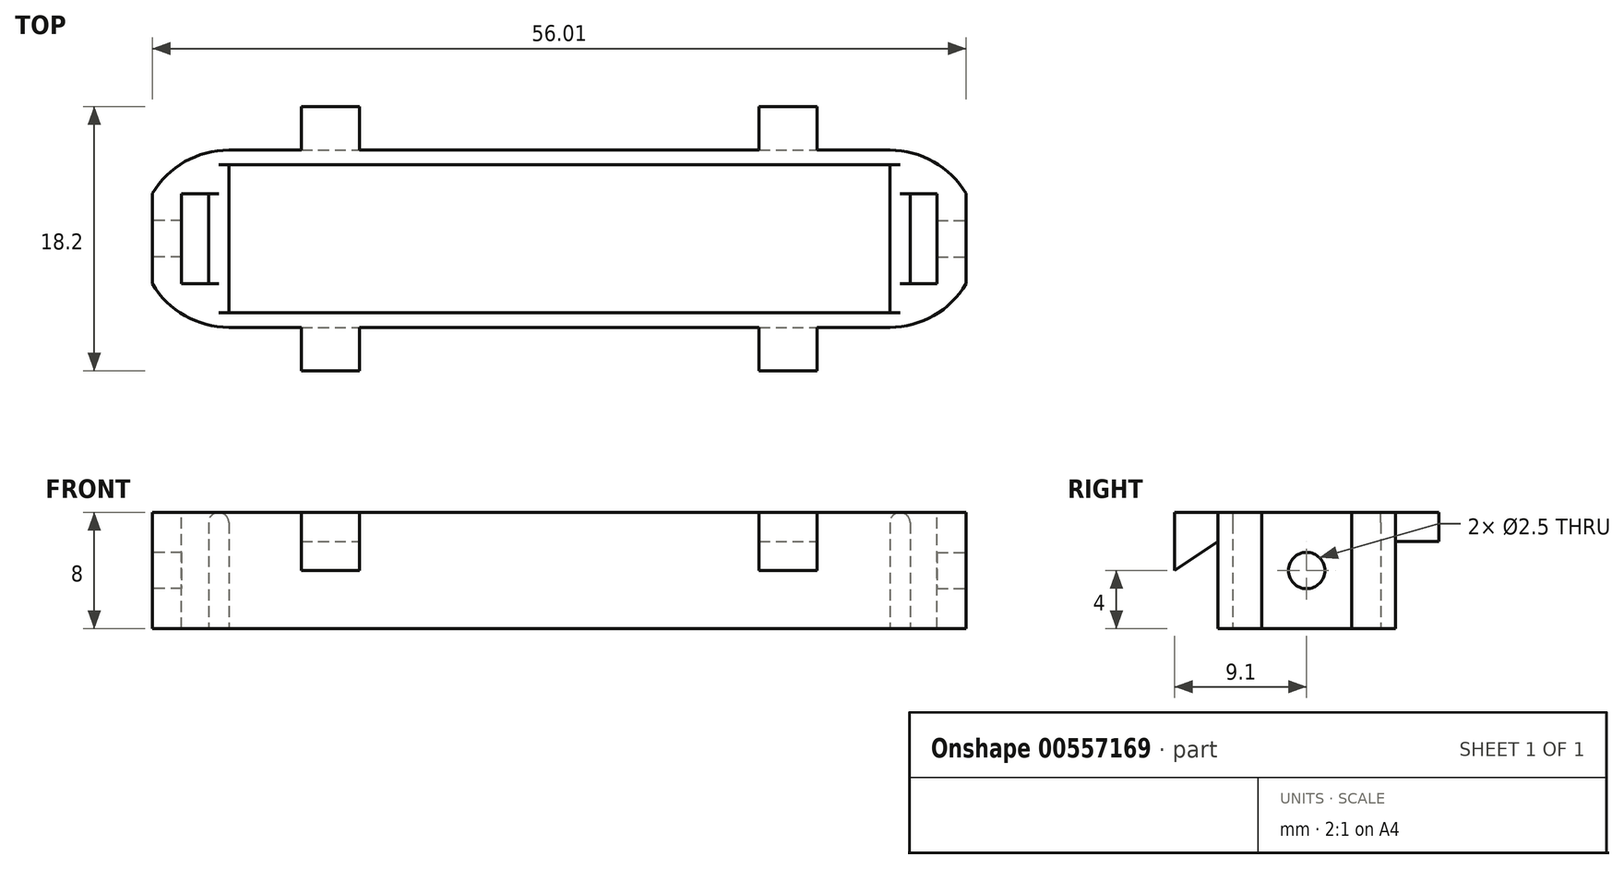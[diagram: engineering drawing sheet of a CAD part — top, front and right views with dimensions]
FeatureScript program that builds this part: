
annotation { "Feature Type Name" : "Feature", "Feature Type Description" : "" }
export const myFeature = defineFeature(function(context is Context, id is Id, definition is map)
    precondition{}
    {
        {
            var Q0;
            Q0=qCreatedBy(makeId("Top.planeOp"),FACE);
            var sketch = newSketch(context, id + "F0", { "sketchPlane" : qUnion([Q0])});
            skLineSegment(sketch, "E0", {"start": v(-58.41, 47.87) * mm, "end": v(-56.91, 47.87) * mm});
            skLineSegment(sketch, "E1", {"start": v(-58.41, 41.67) * mm, "end": v(-56.91, 41.67) * mm});
            skLineSegment(sketch, "E2.trimOffspring", {"start": v(-58.41, 41.67) * mm, "end": v(-58.41, 47.87) * mm});
            skLineSegment(sketch, "E3.trimOffspring", {"start": v(-56.91, 41.67) * mm, "end": v(-56.91, 47.87) * mm});
            skPoint(sketch, "E4", {"position": v(-55.91, 39.67) * mm});
            skPoint(sketch, "E5", {"position": v(-58.41, 44.77) * mm});
            skPoint(sketch, "E6", {"position": v(-55.91, 50.87) * mm});
            skLineSegment(sketch, "E7.MirrorCS", {"start": v(-7.91, 41.67) * mm, "end": v(-9.41, 41.67) * mm});
            skLineSegment(sketch, "E8.MirrorCS", {"start": v(-7.91, 47.87) * mm, "end": v(-9.41, 47.87) * mm});
            skLineSegment(sketch, "E9.MirrorCS", {"start": v(-9.41, 41.67) * mm, "end": v(-9.41, 47.87) * mm});
            skLineSegment(sketch, "E10.MirrorCS", {"start": v(-7.91, 41.67) * mm, "end": v(-7.91, 47.87) * mm});
            skPoint(sketch, "E11.MirrorP", {"position": v(-10.41, 39.67) * mm});
            skPoint(sketch, "E12.MirrorP", {"position": v(-10.41, 50.87) * mm});
            skLineSegment(sketch, "E13", {"start": v(-55.91, 49.87) * mm, "end": v(-10.41, 49.87) * mm});
            skLineSegment(sketch, "E14", {"start": v(-55.91, 50.87) * mm, "end": v(-10.41, 50.87) * mm});
            skLineSegment(sketch, "E15", {"start": v(-55.91, 49.87) * mm, "end": v(-55.91, 39.67) * mm});
            skLineSegment(sketch, "E16", {"start": v(-10.41, 49.87) * mm, "end": v(-10.41, 39.67) * mm});
            skPoint(sketch, "E17", {"position": v(-56.91, 44.77) * mm});
            skPoint(sketch, "E18", {"position": v(-55.91, 44.77) * mm});
            skPoint(sketch, "E19", {"position": v(-9.41, 44.77) * mm});
            skPoint(sketch, "E20", {"position": v(-10.41, 44.77) * mm});
            skLineSegment(sketch, "E21", {"start": v(-55.91, 39.67) * mm, "end": v(-10.41, 39.67) * mm});
            skLineSegment(sketch, "E22", {"start": v(-55.91, 38.67) * mm, "end": v(-10.41, 38.67) * mm});
            skPoint(sketch, "E23", {"position": v(-7.91, 44.77) * mm});
            skPoint(sketch, "E24", {"position": v(-55.91, 38.67) * mm});
            skPoint(sketch, "E25", {"position": v(-10.41, 38.67) * mm});
            skPoint(sketch, "E26", {"position": v(-10.41, 49.87) * mm});
            skPoint(sketch, "E27", {"position": v(-55.91, 49.87) * mm});
            skArc(sketch, "E28", {"start": v(-55.91, 50.87) * mm, "mid": v(-58.94, 50.07) * mm, "end": v(-61.17, 47.88) * mm});
            skArc(sketch, "E29", {"start": v(-10.41, 38.67) * mm, "mid": v(-7.4, 39.47) * mm, "end": v(-5.16, 41.67) * mm});
            skLineSegment(sketch, "E30", {"start": v(-61.17, 47.88) * mm, "end": v(-61.17, 41.67) * mm});
            skPoint(sketch, "E31", {"position": v(-33.16, 50.87) * mm});
            skPoint(sketch, "E32", {"position": v(-33.16, 38.67) * mm});
            skLineSegment(sketch, "E33", {"start": v(-33.16, 50.87) * mm, "end": v(-33.16, 38.67) * mm, "construction": true});
            skLineSegment(sketch, "E34.MirrorCS", {"start": v(-5.16, 47.88) * mm, "end": v(-5.16, 41.67) * mm});
            skArc(sketch, "E35.trimOffspring", {"start": v(-61.17, 41.67) * mm, "mid": v(-58.94, 39.47) * mm, "end": v(-55.91, 38.67) * mm});
            skArc(sketch, "E36.trimOffspring", {"start": v(-5.16, 47.88) * mm, "mid": v(-7.4, 50.07) * mm, "end": v(-10.41, 50.87) * mm});
            skLineSegment(sketch, "E37", {"start": v(-55.91, 44.77) * mm, "end": v(-10.41, 44.77) * mm, "construction": true});
            skSolve(sketch);
        }
        {
            var Q0;
            Q0=makeQuery(id+"F0.imprint","IMPRINT",FACE,{"disambiguationData":[TD([[makeQuery(id+"F0.imprint","IMPRINT",EDGE,{"derivedFrom":sQuery(id+"F0.wireOp",EDGE,"E0")}),1.0]])]});
            extrude(context, id + "F1", {"entities" : qUnion([Q0]), "depth" : 8 * mm, "offsetDistance" : 25 * mm});
        }
        {
            var Q0;
            Q0=makeQuery(id+"F1.opExtrude","SWEPT_FACE",FACE,{"disambiguationData":[OSD([sQuery(id+"F0.wireOp",EDGE,"E34.MirrorCS")])]});
            var sketch = newSketch(context, id + "F2", { "sketchPlane" : qUnion([Q0])});
            skPoint(sketch, "E38.0", {"position": v(44.77, 0) * mm});
            skPoint(sketch, "E38.2", {"position": v(44.77, 0) * mm});
            skCircle(sketch, "E39", {"center": v(44.77, 4) * mm, "radius": 1.25 * mm});
            skPoint(sketch, "E39.centerSnap0", {"position": v(45.62, 4) * mm});
            skSolve(sketch);
        }
        {
            var Q0;
            Q0=makeQuery(id+"F1.opExtrude","SWEPT_FACE",FACE,{"disambiguationData":[OSD([sQuery(id+"F0.wireOp",EDGE,"E30")])]});
            var sketch = newSketch(context, id + "F3", { "sketchPlane" : qUnion([Q0])});
            skPoint(sketch, "E40.0", {"position": v(-44.77, 0) * mm});
            skPoint(sketch, "E41.0", {"position": v(-45.62, 4) * mm});
            skCircle(sketch, "E42", {"center": v(-44.77, 4) * mm, "radius": 1.25 * mm});
            skSolve(sketch);
        }
        {
            var Q0;
            Q0=makeQuery(id+"F3.imprint","IMPRINT",FACE,{"disambiguationData":[TD([[makeQuery(id+"F3.imprint","IMPRINT",EDGE,{"derivedFrom":sQuery(id+"F3.wireOp",EDGE,"E42")}),1.0]])]});
            extrude(context, id + "F4", {"entities" : qUnion([Q0]), "operationType" : NewBodyOperationType.REMOVE, "oppositeDirection" : true, "depth" : 3 * mm, "offsetDistance" : 25 * mm});
        }
        {
            var Q0;
            Q0=makeQuery(id+"F2.imprint","IMPRINT",FACE,{"disambiguationData":[TD([[makeQuery(id+"F2.imprint","IMPRINT",EDGE,{"derivedFrom":sQuery(id+"F2.wireOp",EDGE,"E39")}),1.0]])]});
            extrude(context, id + "F5", {"entities" : qUnion([Q0]), "operationType" : NewBodyOperationType.REMOVE, "oppositeDirection" : true, "depth" : 3 * mm, "offsetDistance" : 25 * mm});
        }
        {
            var Q0;
            Q0=makeQuery(id+"F1.opExtrude","CAP_FACE",FACE,{"disambiguationData":[OSD([sQuery(id+"F0.wireOp",EDGE,"5c85485d-57c3-49a4-9234-01fc0bf89ff7.left"),sQuery(id+"F0.wireOp",EDGE,"5c85485d-57c3-49a4-9234-01fc0bf89ff7.right"),sQuery(id+"F0.wireOp",EDGE,"E0"),sQuery(id+"F0.wireOp",EDGE,"E1"),sQuery(id+"F0.wireOp",EDGE,"f26dac97-f157-4d3b-b19c-ac2ae7369aeb.MirrorCS"),sQuery(id+"F0.wireOp",EDGE,"fdaca539-c827-4bf9-9b72-cb5319b9078c.MirrorCS"),sQuery(id+"F0.wireOp",EDGE,"E2.trimOffspring"),sQuery(id+"F0.wireOp",EDGE,"E3.trimOffspring"),sQuery(id+"F0.wireOp",EDGE,"773fe0d1-a9d3-4c5f-a97c-df7c8a0fcf99"),sQuery(id+"F0.wireOp",EDGE,"c1d238ae-af6c-4615-ba33-6711a1cbf2eb.MirrorCS"),sQuery(id+"F0.wireOp",EDGE,"24cf176b-f46d-4737-b83f-17166a3a977d"),sQuery(id+"F0.wireOp",EDGE,"930f735f-535e-48a8-9612-ca19f04ff2fe.MirrorCS"),sQuery(id+"F0.wireOp",EDGE,"54351eae-afcf-4464-b00b-301f5b7c95d1.MirrorCS"),sQuery(id+"F0.wireOp",EDGE,"E7.MirrorCS"),sQuery(id+"F0.wireOp",EDGE,"E8.MirrorCS"),sQuery(id+"F0.wireOp",EDGE,"E10.MirrorCS"),sQuery(id+"F0.wireOp",EDGE,"2c25c5c6-e33a-4382-b5a6-a77b0c508d72.MirrorCS"),sQuery(id+"F0.wireOp",EDGE,"f8cf7686-dc48-4d1f-ad7e-551f82504d00.MirrorCS"),sQuery(id+"F0.wireOp",EDGE,"E9.MirrorCS"),sQuery(id+"F0.wireOp",EDGE,"bb7f4395-c74a-4e4d-ba5c-67a6b84b5c23.MirrorCS"),sQuery(id+"F0.wireOp",EDGE,"2b76229e-1219-44ec-801c-a60a5f2764bf.MirrorCS"),sQuery(id+"F0.wireOp",EDGE,"5ebec35d-3fc7-4fed-b7fb-ec59319a5e31.MirrorCS"),sQuery(id+"F0.wireOp",EDGE,"E13"),sQuery(id+"F0.wireOp",EDGE,"E14"),sQuery(id+"F0.wireOp",EDGE,"nzgn4MnC-cCwg-rH8m-cCMt-Htn1G1sgsl9W"),sQuery(id+"F0.wireOp",EDGE,"OD229cqR-pfQO-gkFn-DRH1-wKdn3JZuODgv"),sQuery(id+"F0.wireOp",EDGE,"E15"),sQuery(id+"F0.wireOp",EDGE,"E16")])],"isStart":false});
            var sketch = newSketch(context, id + "F6", { "sketchPlane" : qUnion([Q0])});
            skPoint(sketch, "E43", {"position": v(-33.16, 50.87) * mm});
            skLineSegment(sketch, "E44", {"start": v(-55.91, 44.77) * mm, "end": v(-10.41, 44.77) * mm, "construction": true});
            skPoint(sketch, "E45.0", {"position": v(-55.91, 50.87) * mm});
            skPoint(sketch, "E45.1", {"position": v(-10.41, 50.87) * mm});
            skPoint(sketch, "E46", {"position": v(-17.41, 50.87) * mm});
            skPoint(sketch, "E47", {"position": v(-48.91, 50.87) * mm});
            skLineSegment(sketch, "E48", {"start": v(-19.41, 53.87) * mm, "end": v(-19.41, 50.87) * mm});
            skLineSegment(sketch, "E49", {"start": v(-15.41, 53.87) * mm, "end": v(-15.41, 50.87) * mm});
            skLineSegment(sketch, "E50", {"start": v(-19.41, 53.87) * mm, "end": v(-15.41, 53.87) * mm});
            skLineSegment(sketch, "E51.MirrorCS", {"start": v(-15.41, 35.67) * mm, "end": v(-15.41, 38.67) * mm});
            skLineSegment(sketch, "E52.MirrorCS", {"start": v(-19.41, 35.67) * mm, "end": v(-19.41, 38.67) * mm});
            skLineSegment(sketch, "E53.MirrorCS", {"start": v(-19.41, 35.67) * mm, "end": v(-15.41, 35.67) * mm});
            skLineSegment(sketch, "E54.MirrorCS", {"start": v(-46.91, 53.87) * mm, "end": v(-46.91, 50.87) * mm});
            skLineSegment(sketch, "E55.MirrorCS", {"start": v(-46.91, 53.87) * mm, "end": v(-50.91, 53.87) * mm});
            skLineSegment(sketch, "E56.MirrorCS", {"start": v(-50.91, 53.87) * mm, "end": v(-50.91, 50.87) * mm});
            skLineSegment(sketch, "E57.MirrorCS", {"start": v(-50.91, 35.67) * mm, "end": v(-50.91, 38.67) * mm});
            skLineSegment(sketch, "E58.MirrorCS", {"start": v(-46.91, 35.67) * mm, "end": v(-50.91, 35.67) * mm});
            skLineSegment(sketch, "E59.MirrorCS", {"start": v(-46.91, 35.67) * mm, "end": v(-46.91, 38.67) * mm});
            skSolve(sketch);
        }
        {
            var Q0;
            {var subQ0=sQuery(id+"F6.wireOp",EDGE,"E48");Q0=makeQuery(id+"F6.imprint","IMPRINT",FACE,{"disambiguationData":[TD([[makeQuery(id+"F6.imprint","IMPRINT",EDGE,{"derivedFrom":subQ0}),1.0]])]});}
            var Q1;
            {var subQ0=sQuery(id+"F6.wireOp",EDGE,"E54.MirrorCS");Q1=makeQuery(id+"F6.imprint","IMPRINT",FACE,{"disambiguationData":[TD([[makeQuery(id+"F6.imprint","IMPRINT",EDGE,{"derivedFrom":subQ0}),-1.0]])]});}
            var Q2;
            {var subQ0=sQuery(id+"F6.wireOp",EDGE,"E57.MirrorCS");Q2=makeQuery(id+"F6.imprint","IMPRINT",FACE,{"disambiguationData":[TD([[makeQuery(id+"F6.imprint","IMPRINT",EDGE,{"derivedFrom":subQ0}),-1.0]])]});}
            var Q3;
            {var subQ0=sQuery(id+"F6.wireOp",EDGE,"E51.MirrorCS");Q3=makeQuery(id+"F6.imprint","IMPRINT",FACE,{"disambiguationData":[TD([[makeQuery(id+"F6.imprint","IMPRINT",EDGE,{"derivedFrom":subQ0}),1.0]])]});}
            extrude(context, id + "F7", {"entities" : qUnion([Q0, Q1, Q2, Q3]), "operationType" : NewBodyOperationType.ADD, "oppositeDirection" : true, "depth" : 2 * mm, "offsetDistance" : 25 * mm});
        }
        {
            var Q0;
            Q0=makeQuery(id+"F7.opExtrude","SWEPT_FACE",FACE,{"disambiguationData":[OSD([sQuery(id+"F6.wireOp",EDGE,"E51.MirrorCS")])]});
            var sketch = newSketch(context, id + "F8", { "sketchPlane" : qUnion([Q0])});
            skPoint(sketch, "E60", {"position": v(35.67, 4) * mm});
            skLineSegment(sketch, "E61", {"start": v(35.67, 6) * mm, "end": v(35.67, 4) * mm});
            skLineSegment(sketch, "E62", {"start": v(35.67, 4) * mm, "end": v(38.67, 6) * mm});
            skSolve(sketch);
        }
        {
            var Q0;
            Q0=makeQuery(id+"F8.imprint","IMPRINT",FACE,{"disambiguationData":[TD([[makeQuery(id+"F8.imprint","IMPRINT",EDGE,{"derivedFrom":sQuery(id+"F8.wireOp",EDGE,"E61")}),1.0]])]});
            extrude(context, id + "F9", {"entities" : qUnion([Q0]), "operationType" : NewBodyOperationType.ADD, "oppositeDirection" : true, "depth" : 4 * mm, "offsetDistance" : 25 * mm});
        }
        {
            var Q0;
            Q0=sQuery(id+"F6.wireOp",EDGE,"E44");
            cPlane(context, id + "F10", {"entities" : qUnion([Q0]), "cplaneType" : CPlaneType.LINE_ANGLE, "offset" : 25 * mm, "angle" : 0 * degree, "width" : 150 * mm, "height" : 150 * mm});
        }
        {
            var Q0;
            Q0=makeQuery(id+"F7.opExtrude","SWEPT_FACE",FACE,{"disambiguationData":[OSD([sQuery(id+"F6.wireOp",EDGE,"E57.MirrorCS")])]});
            var sketch = newSketch(context, id + "F11", { "sketchPlane" : qUnion([Q0])});
            skPoint(sketch, "E63", {"position": v(-35.67, 4) * mm});
            skLineSegment(sketch, "E64", {"start": v(-35.67, 4) * mm, "end": v(-35.67, 6) * mm});
            skLineSegment(sketch, "E65", {"start": v(-35.67, 4) * mm, "end": v(-38.67, 6) * mm});
            skSolve(sketch);
        }
        {
            var Q0;
            Q0=makeQuery(id+"F11.imprint","IMPRINT",FACE,{"disambiguationData":[TD([[makeQuery(id+"F11.imprint","IMPRINT",EDGE,{"derivedFrom":sQuery(id+"F11.wireOp",EDGE,"E64")}),1.0]])]});
            extrude(context, id + "F12", {"entities" : qUnion([Q0]), "operationType" : NewBodyOperationType.ADD, "oppositeDirection" : true, "depth" : 4 * mm, "offsetDistance" : 25 * mm});
        }
        {
            var Q0;
            {var subQ0=sQuery(id+"F0.wireOp",EDGE,"E22");var subQ1=sQuery(id+"F0.wireOp",EDGE,"E14");Q0=makeQuery(id+"F7.boolean.opBoolean","MERGE",FACE,{"derivedFrom":[makeQuery(id+"F1.opExtrude","CAP_FACE",FACE,{"disambiguationData":[OSD([sQuery(id+"F0.wireOp",EDGE,"E0"),sQuery(id+"F0.wireOp",EDGE,"E1"),sQuery(id+"F0.wireOp",EDGE,"E2.trimOffspring"),sQuery(id+"F0.wireOp",EDGE,"E3.trimOffspring"),sQuery(id+"F0.wireOp",EDGE,"E7.MirrorCS"),sQuery(id+"F0.wireOp",EDGE,"E8.MirrorCS"),sQuery(id+"F0.wireOp",EDGE,"E10.MirrorCS"),sQuery(id+"F0.wireOp",EDGE,"E9.MirrorCS"),sQuery(id+"F0.wireOp",EDGE,"E13"),subQ1,sQuery(id+"F0.wireOp",EDGE,"E15"),sQuery(id+"F0.wireOp",EDGE,"E16"),sQuery(id+"F0.wireOp",EDGE,"E21"),subQ0,sQuery(id+"F0.wireOp",EDGE,"E28"),sQuery(id+"F0.wireOp",EDGE,"E29"),sQuery(id+"F0.wireOp",EDGE,"E30"),sQuery(id+"F0.wireOp",EDGE,"E34.MirrorCS"),sQuery(id+"F0.wireOp",EDGE,"E35.trimOffspring"),sQuery(id+"F0.wireOp",EDGE,"E36.trimOffspring")])],"isStart":false}),makeQuery(id+"F7.opExtrude","CAP_FACE",FACE,{"disambiguationData":[OSD([subQ1,sQuery(id+"F6.wireOp",EDGE,"E48"),sQuery(id+"F6.wireOp",EDGE,"E49"),sQuery(id+"F6.wireOp",EDGE,"E50")])],"isStart":true}),makeQuery(id+"F7.opExtrude","CAP_FACE",FACE,{"disambiguationData":[OSD([subQ0,sQuery(id+"F6.wireOp",EDGE,"E51.MirrorCS"),sQuery(id+"F6.wireOp",EDGE,"E52.MirrorCS"),sQuery(id+"F6.wireOp",EDGE,"E53.MirrorCS")])],"isStart":true}),makeQuery(id+"F7.opExtrude","CAP_FACE",FACE,{"disambiguationData":[OSD([subQ1,sQuery(id+"F6.wireOp",EDGE,"E54.MirrorCS"),sQuery(id+"F6.wireOp",EDGE,"E55.MirrorCS"),sQuery(id+"F6.wireOp",EDGE,"E56.MirrorCS")])],"isStart":true}),makeQuery(id+"F7.opExtrude","CAP_FACE",FACE,{"disambiguationData":[OSD([subQ0,sQuery(id+"F6.wireOp",EDGE,"E57.MirrorCS"),sQuery(id+"F6.wireOp",EDGE,"E58.MirrorCS"),sQuery(id+"F6.wireOp",EDGE,"E59.MirrorCS")])],"isStart":true})]});}
            var sketch = newSketch(context, id + "F13", { "sketchPlane" : qUnion([Q0])});
            skLineSegment(sketch, "E66.0", {"start": v(-56.91, 41.67) * mm, "end": v(-56.91, 47.87) * mm});
            skLineSegment(sketch, "E66.1", {"start": v(-58.41, 47.87) * mm, "end": v(-56.91, 47.87) * mm});
            skLineSegment(sketch, "E66.2", {"start": v(-58.41, 41.67) * mm, "end": v(-58.41, 47.87) * mm});
            skLineSegment(sketch, "E66.3", {"start": v(-58.41, 41.67) * mm, "end": v(-56.91, 41.67) * mm});
            skLineSegment(sketch, "E67.0", {"start": v(-7.91, 47.87) * mm, "end": v(-9.41, 47.87) * mm});
            skLineSegment(sketch, "E67.1", {"start": v(-7.91, 41.67) * mm, "end": v(-7.91, 47.87) * mm});
            skLineSegment(sketch, "E67.2", {"start": v(-9.41, 41.67) * mm, "end": v(-9.41, 47.87) * mm});
            skLineSegment(sketch, "E67.3", {"start": v(-7.91, 41.67) * mm, "end": v(-9.41, 41.67) * mm});
            skLineSegment(sketch, "E68", {"start": v(-58.41, 47.87) * mm, "end": v(-59.16, 47.87) * mm});
            skLineSegment(sketch, "E69", {"start": v(-59.16, 47.87) * mm, "end": v(-59.16, 41.67) * mm});
            skLineSegment(sketch, "E70", {"start": v(-59.16, 41.67) * mm, "end": v(-58.41, 41.67) * mm});
            skLineSegment(sketch, "E71", {"start": v(-7.91, 47.87) * mm, "end": v(-7.16, 47.87) * mm});
            skLineSegment(sketch, "E72", {"start": v(-7.16, 47.87) * mm, "end": v(-7.16, 41.67) * mm});
            skLineSegment(sketch, "E73", {"start": v(-7.16, 41.67) * mm, "end": v(-7.91, 41.67) * mm});
            skSolve(sketch);
        }
        {
            var Q0;
            Q0=makeQuery(id+"F13.imprint","IMPRINT",FACE,{"disambiguationData":[TD([[makeQuery(id+"F13.imprint","IMPRINT",EDGE,{"derivedFrom":sQuery(id+"F13.wireOp",EDGE,"E66.2")}),1.0]])]});
            var Q1;
            Q1=makeQuery(id+"F13.imprint","IMPRINT",FACE,{"disambiguationData":[TD([[makeQuery(id+"F13.imprint","IMPRINT",EDGE,{"derivedFrom":sQuery(id+"F13.wireOp",EDGE,"E67.1")}),-1.0]])]});
            extrude(context, id + "F14", {"entities" : qUnion([Q0, Q1]), "operationType" : NewBodyOperationType.REMOVE, "endBound" : BoundingType.THROUGH_ALL, "oppositeDirection" : true, "depth" : 25 * mm, "offsetDistance" : 25 * mm});
        }
        {
            var Q0;
            Q0=makeQuery(id+"F1.opExtrude","SWEPT_FACE",FACE,{"disambiguationData":[OSD([sQuery(id+"F0.wireOp",EDGE,"E3.trimOffspring")])]});
            extrude(context, id + "F15", {"entities" : qUnion([Q0]), "operationType" : NewBodyOperationType.ADD, "depth" : .4 * mm, "offsetDistance" : 25 * mm});
        }
        {
            var Q0;
            Q0=makeQuery(id+"F1.opExtrude","SWEPT_FACE",FACE,{"disambiguationData":[OSD([sQuery(id+"F0.wireOp",EDGE,"E9.MirrorCS")])]});
            extrude(context, id + "F16", {"entities" : qUnion([Q0]), "operationType" : NewBodyOperationType.ADD, "depth" : .4 * mm, "offsetDistance" : 25 * mm});
        }
        {
            var Q0;
            Q0=makeQuery(id+"F1.opExtrude","CAP_EDGE",EDGE,{"disambiguationData":[OSD([sQuery(id+"F0.wireOp",EDGE,"E15")])],"isStart":false});
            var Q1;
            {var subQ0=sQuery(id+"F0.wireOp",EDGE,"E3.trimOffspring");Q1=makeQuery(id+"F15.opExtrude","CAP_EDGE",EDGE,{"disambiguationData":[OSD([subQ0]),TDD([makeQuery(id+"F1.opExtrude","CAP_EDGE",EDGE,{"disambiguationData":[OSD([subQ0])],"isStart":false})])],"isStart":false});}
            fillet(context, id + "F17", {"entities" : qUnion([Q0, Q1]), "radius" : .7 * mm, "tangentPropagation" : true, "allowEdgeOverflow" : false});
        }
        {
            var Q0;
            {var subQ0=sQuery(id+"F0.wireOp",EDGE,"E9.MirrorCS");Q0=makeQuery(id+"F16.opExtrude","CAP_EDGE",EDGE,{"disambiguationData":[OSD([subQ0]),TDD([makeQuery(id+"F1.opExtrude","CAP_EDGE",EDGE,{"disambiguationData":[OSD([subQ0])],"isStart":false})])],"isStart":false});}
            var Q1;
            Q1=makeQuery(id+"F1.opExtrude","CAP_EDGE",EDGE,{"disambiguationData":[OSD([sQuery(id+"F0.wireOp",EDGE,"E16")])],"isStart":false});
            fillet(context, id + "F18", {"entities" : qUnion([Q0, Q1]), "radius" : .7 * mm, "tangentPropagation" : true, "allowEdgeOverflow" : false});
        }
    });
